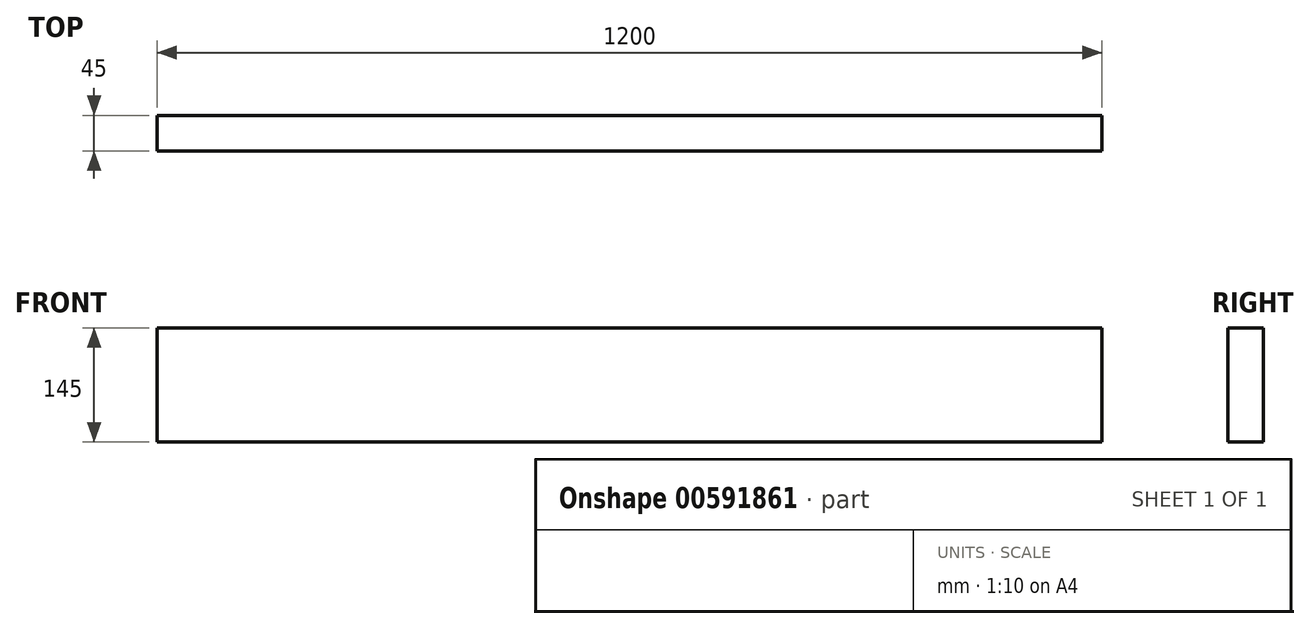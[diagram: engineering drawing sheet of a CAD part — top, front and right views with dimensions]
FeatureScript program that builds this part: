
annotation { "Feature Type Name" : "Feature", "Feature Type Description" : "" }
export const myFeature = defineFeature(function(context is Context, id is Id, definition is map)
    precondition{}
    {
        {
            var Q0;
            Q0=qCreatedBy(makeId("Front.planeOp"),FACE);
            var sketch = newSketch(context, id + "F0", { "sketchPlane" : qUnion([Q0])});
            skLineSegment(sketch, "E0.bottom", {"start": v(0, 0) * mm, "end": v(1200, 0) * mm});
            skLineSegment(sketch, "E0.top", {"start": v(0, 145) * mm, "end": v(1200, 145) * mm});
            skLineSegment(sketch, "E0.left", {"start": v(0, 0) * mm, "end": v(0, 145) * mm});
            skLineSegment(sketch, "E0.right", {"start": v(1200, 0) * mm, "end": v(1200, 145) * mm});
            skSolve(sketch);
        }
        {
            var Q0;
            Q0=makeQuery(id+"F0.imprint","IMPRINT",FACE,{"disambiguationData":[TD([[makeQuery(id+"F0.imprint","IMPRINT",EDGE,{"derivedFrom":sQuery(id+"F0.wireOp",EDGE,"E0.bottom")}),1.0]])]});
            extrude(context, id + "F1", {"entities" : qUnion([Q0]), "depth" : 45 * mm, "offsetDistance" : 25 * mm});
        }
    });
